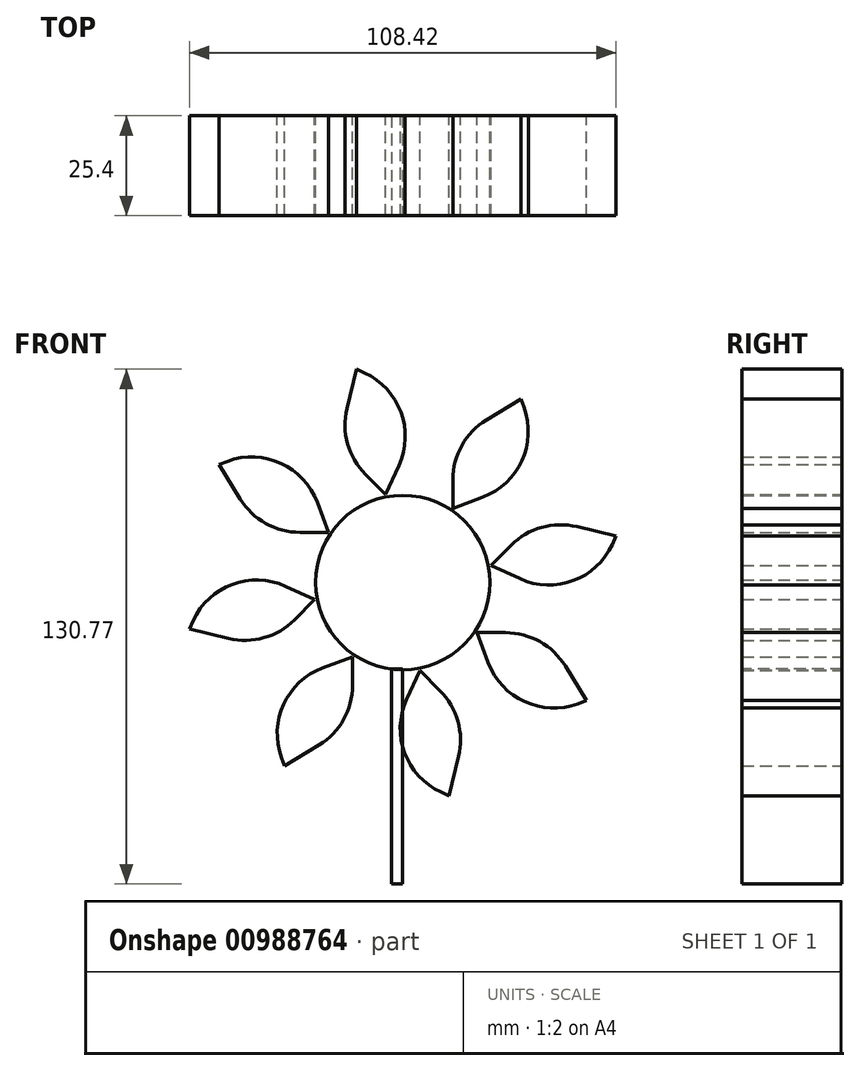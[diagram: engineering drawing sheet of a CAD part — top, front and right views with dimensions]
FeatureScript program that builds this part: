
annotation { "Feature Type Name" : "Feature", "Feature Type Description" : "" }
export const myFeature = defineFeature(function(context is Context, id is Id, definition is map)
    precondition{}
    {
        {
            var Q0;
            Q0=qCreatedBy(makeId("Front.planeOp"),FACE);
            var sketch = newSketch(context, id + "F0", { "sketchPlane" : qUnion([Q0])});
            skCircle(sketch, "E0", {"center": v(0, 0) * mm, "radius": 22.15 * mm});
            skSolve(sketch);
        }
        {
            var Q0;
            Q0=makeQuery(id+"F0.imprint","IMPRINT",FACE,{"disambiguationData":[TD([[makeQuery(id+"F0.imprint","IMPRINT",EDGE,{"derivedFrom":sQuery(id+"F0.wireOp",EDGE,"E0")}),1.0]])]});
            var sketch = newSketch(context, id + "F1", { "sketchPlane" : qUnion([Q0])});
            skLineSegment(sketch, "E1", {"start": v(12.74, 18.87) * mm, "end": v(12.74, 26.13) * mm});
            skLineSegment(sketch, "E2", {"start": v(21.25, 41.3) * mm, "end": v(30, 46.65) * mm});
            skLineSegment(sketch, "E3", {"start": v(30, 46.65) * mm, "end": v(30.79, 44.53) * mm});
            skLineSegment(sketch, "E4", {"start": v(20.33, 21.7) * mm, "end": v(12.74, 18.87) * mm});
            skPoint(sketch, "E5.visualSharp", {"position": v(12.74, 36.1) * mm});
            skArc(sketch, "E5.filletArc", {"start": v(21.25, 41.3) * mm, "mid": v(15.02, 34.83) * mm, "end": v(12.74, 26.13) * mm});
            skPoint(sketch, "E6.visualSharp", {"position": v(36.94, 27.9) * mm});
            skArc(sketch, "E6.filletArc", {"start": v(20.33, 21.7) * mm, "mid": v(30.28, 30.96) * mm, "end": v(30.79, 44.53) * mm});
            skLineSegment(sketch, "E7.1.0", {"start": v(-11.77, 54.2) * mm, "end": v(-9.72, 53.26) * mm});
            skLineSegment(sketch, "E7.1.1", {"start": v(-14.18, 44.23) * mm, "end": v(-11.77, 54.2) * mm});
            skArc(sketch, "E7.1.2", {"start": v(-0.97, 29.73) * mm, "mid": v(-0.48, 43.3) * mm, "end": v(-9.72, 53.26) * mm});
            skLineSegment(sketch, "E7.1.3", {"start": v(-0.97, 29.73) * mm, "end": v(-4.33, 22.36) * mm});
            skLineSegment(sketch, "E7.1.4", {"start": v(-4.33, 22.36) * mm, "end": v(-9.47, 27.5) * mm});
            skArc(sketch, "E7.1.5", {"start": v(-14.18, 44.23) * mm, "mid": v(-14.01, 35.25) * mm, "end": v(-9.47, 27.5) * mm});
            skLineSegment(sketch, "E7.2.0", {"start": v(-46.65, 30) * mm, "end": v(-44.53, 30.79) * mm});
            skLineSegment(sketch, "E7.2.1", {"start": v(-41.3, 21.25) * mm, "end": v(-46.65, 30) * mm});
            skArc(sketch, "E7.2.2", {"start": v(-21.7, 20.33) * mm, "mid": v(-30.96, 30.28) * mm, "end": v(-44.53, 30.79) * mm});
            skLineSegment(sketch, "E7.2.3", {"start": v(-21.7, 20.33) * mm, "end": v(-18.87, 12.74) * mm});
            skLineSegment(sketch, "E7.2.4", {"start": v(-18.87, 12.74) * mm, "end": v(-26.13, 12.74) * mm});
            skArc(sketch, "E7.2.5", {"start": v(-41.3, 21.25) * mm, "mid": v(-34.83, 15.02) * mm, "end": v(-26.13, 12.74) * mm});
            skLineSegment(sketch, "E7.3.0", {"start": v(-54.2, -11.77) * mm, "end": v(-53.26, -9.72) * mm});
            skLineSegment(sketch, "E7.3.1", {"start": v(-44.23, -14.18) * mm, "end": v(-54.2, -11.77) * mm});
            skArc(sketch, "E7.3.2", {"start": v(-29.73, -0.97) * mm, "mid": v(-43.3, -0.48) * mm, "end": v(-53.26, -9.72) * mm});
            skLineSegment(sketch, "E7.3.3", {"start": v(-29.73, -0.97) * mm, "end": v(-22.36, -4.33) * mm});
            skLineSegment(sketch, "E7.3.4", {"start": v(-22.36, -4.33) * mm, "end": v(-27.5, -9.47) * mm});
            skArc(sketch, "E7.3.5", {"start": v(-44.23, -14.18) * mm, "mid": v(-35.25, -14.01) * mm, "end": v(-27.5, -9.47) * mm});
            skLineSegment(sketch, "E7.4.0", {"start": v(-30, -46.65) * mm, "end": v(-30.79, -44.53) * mm});
            skLineSegment(sketch, "E7.4.1", {"start": v(-21.25, -41.3) * mm, "end": v(-30, -46.65) * mm});
            skArc(sketch, "E7.4.2", {"start": v(-20.33, -21.7) * mm, "mid": v(-30.28, -30.96) * mm, "end": v(-30.79, -44.53) * mm});
            skLineSegment(sketch, "E7.4.3", {"start": v(-20.33, -21.7) * mm, "end": v(-12.74, -18.87) * mm});
            skLineSegment(sketch, "E7.4.4", {"start": v(-12.74, -18.87) * mm, "end": v(-12.74, -26.13) * mm});
            skArc(sketch, "E7.4.5", {"start": v(-21.25, -41.3) * mm, "mid": v(-15.02, -34.83) * mm, "end": v(-12.74, -26.13) * mm});
            skLineSegment(sketch, "E7.5.0", {"start": v(11.77, -54.2) * mm, "end": v(9.72, -53.26) * mm});
            skLineSegment(sketch, "E7.5.1", {"start": v(14.18, -44.23) * mm, "end": v(11.77, -54.2) * mm});
            skArc(sketch, "E7.5.2", {"start": v(0.97, -29.73) * mm, "mid": v(0.48, -43.3) * mm, "end": v(9.72, -53.26) * mm});
            skLineSegment(sketch, "E7.5.3", {"start": v(0.97, -29.73) * mm, "end": v(4.33, -22.36) * mm});
            skLineSegment(sketch, "E7.5.4", {"start": v(4.33, -22.36) * mm, "end": v(9.47, -27.5) * mm});
            skArc(sketch, "E7.5.5", {"start": v(14.18, -44.23) * mm, "mid": v(14.01, -35.25) * mm, "end": v(9.47, -27.5) * mm});
            skLineSegment(sketch, "E7.6.0", {"start": v(46.65, -30) * mm, "end": v(44.53, -30.79) * mm});
            skLineSegment(sketch, "E7.6.1", {"start": v(41.3, -21.25) * mm, "end": v(46.65, -30) * mm});
            skArc(sketch, "E7.6.2", {"start": v(21.7, -20.33) * mm, "mid": v(30.96, -30.28) * mm, "end": v(44.53, -30.79) * mm});
            skLineSegment(sketch, "E7.6.3", {"start": v(21.7, -20.33) * mm, "end": v(18.87, -12.74) * mm});
            skLineSegment(sketch, "E7.6.4", {"start": v(18.87, -12.74) * mm, "end": v(26.13, -12.74) * mm});
            skArc(sketch, "E7.6.5", {"start": v(41.3, -21.25) * mm, "mid": v(34.83, -15.02) * mm, "end": v(26.13, -12.74) * mm});
            skLineSegment(sketch, "E7.7.0", {"start": v(54.2, 11.77) * mm, "end": v(53.26, 9.72) * mm});
            skLineSegment(sketch, "E7.7.1", {"start": v(44.23, 14.18) * mm, "end": v(54.2, 11.77) * mm});
            skArc(sketch, "E7.7.2", {"start": v(29.73, 0.97) * mm, "mid": v(43.3, 0.48) * mm, "end": v(53.26, 9.72) * mm});
            skLineSegment(sketch, "E7.7.3", {"start": v(29.73, 0.97) * mm, "end": v(22.36, 4.33) * mm});
            skLineSegment(sketch, "E7.7.4", {"start": v(22.36, 4.33) * mm, "end": v(27.5, 9.47) * mm});
            skArc(sketch, "E7.7.5", {"start": v(44.23, 14.18) * mm, "mid": v(35.25, 14.01) * mm, "end": v(27.5, 9.47) * mm});
            skPoint(sketch, "E7.center", {"position": v(0, 0) * mm});
            skSolve(sketch);
        }
        {
            var Q0;
            Q0=makeQuery(id+"F1.imprint","IMPRINT",FACE,{"disambiguationData":[TD([[makeQuery(id+"F1.imprint","IMPRINT",EDGE,{"derivedFrom":sQuery(id+"F1.wireOp",EDGE,"E1")}),-1.0]])]});
            var Q1;
            Q1=makeQuery(id+"F1.imprint","IMPRINT",FACE,{"disambiguationData":[TD([[makeQuery(id+"F1.imprint","IMPRINT",EDGE,{"derivedFrom":sQuery(id+"F1.wireOp",EDGE,"E7.1.0")}),-1.0]])]});
            var Q2;
            Q2=makeQuery(id+"F1.imprint","IMPRINT",FACE,{"disambiguationData":[TD([[makeQuery(id+"F1.imprint","IMPRINT",EDGE,{"derivedFrom":sQuery(id+"F1.wireOp",EDGE,"E7.2.0")}),-1.0]])]});
            var Q3;
            Q3=makeQuery(id+"F0.imprint","IMPRINT",FACE,{"disambiguationData":[TD([[makeQuery(id+"F0.imprint","IMPRINT",EDGE,{"derivedFrom":sQuery(id+"F0.wireOp",EDGE,"E0")}),1.0]])]});
            var Q4;
            Q4=makeQuery(id+"F1.imprint","IMPRINT",FACE,{"disambiguationData":[TD([[makeQuery(id+"F1.imprint","IMPRINT",EDGE,{"derivedFrom":sQuery(id+"F1.wireOp",EDGE,"E7.7.0")}),-1.0]])]});
            var Q5;
            Q5=makeQuery(id+"F1.imprint","IMPRINT",FACE,{"disambiguationData":[TD([[makeQuery(id+"F1.imprint","IMPRINT",EDGE,{"derivedFrom":sQuery(id+"F1.wireOp",EDGE,"E7.6.0")}),-1.0]])]});
            var Q6;
            Q6=makeQuery(id+"F1.imprint","IMPRINT",FACE,{"disambiguationData":[TD([[makeQuery(id+"F1.imprint","IMPRINT",EDGE,{"derivedFrom":sQuery(id+"F1.wireOp",EDGE,"E7.5.0")}),-1.0]])]});
            var Q7;
            Q7=makeQuery(id+"F1.imprint","IMPRINT",FACE,{"disambiguationData":[TD([[makeQuery(id+"F1.imprint","IMPRINT",EDGE,{"derivedFrom":sQuery(id+"F1.wireOp",EDGE,"E7.4.0")}),-1.0]])]});
            var Q8;
            Q8=makeQuery(id+"F1.imprint","IMPRINT",FACE,{"disambiguationData":[TD([[makeQuery(id+"F1.imprint","IMPRINT",EDGE,{"derivedFrom":sQuery(id+"F1.wireOp",EDGE,"E7.3.0")}),-1.0]])]});
            extrude(context, id + "F2", {"entities" : qUnion([Q0, Q1, Q2, Q3, Q4, Q5, Q6, Q7, Q8]), "depth" : 25.4 * mm, "offsetDistance" : 25.4 * mm});
        }
        {
            var Q0;
            Q0=makeQuery(id+"F2.opExtrude","CAP_FACE",FACE,{"disambiguationData":[OSD([sQuery(id+"F0.wireOp",EDGE,"E0")])],"isStart":false});
            var sketch = newSketch(context, id + "F3", { "sketchPlane" : qUnion([Q0])});
            skLineSegment(sketch, "E8.bottom", {"start": v(-2.83, -21.97) * mm, "end": v(0, -21.97) * mm});
            skLineSegment(sketch, "E8.top", {"start": v(-2.83, -76.56) * mm, "end": v(0, -76.56) * mm});
            skLineSegment(sketch, "E8.left", {"start": v(-2.83, -21.97) * mm, "end": v(-2.83, -76.56) * mm});
            skLineSegment(sketch, "E8.right", {"start": v(0, -21.97) * mm, "end": v(0, -76.56) * mm});
            skSolve(sketch);
        }
        {
            var Q0;
            Q0 = qSketchRegion(id + "F3", true);
            extrude(context, id + "F4", {"entities" : qUnion([Q0]), "oppositeDirection" : true, "depth" : 25.4 * mm, "offsetDistance" : 25.4 * mm});
        }
    });
